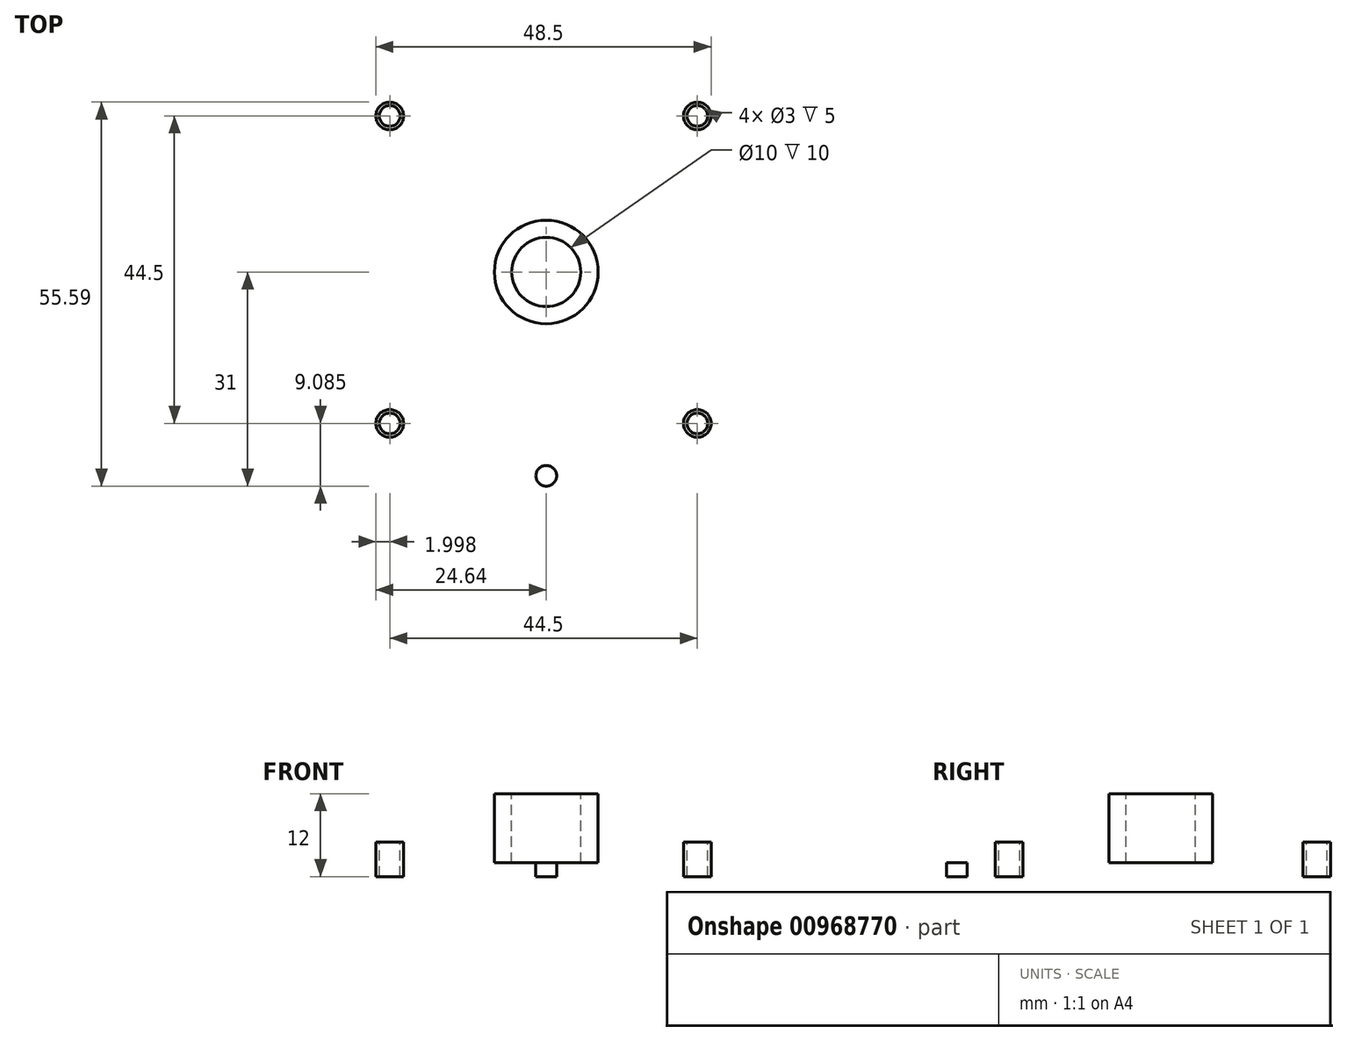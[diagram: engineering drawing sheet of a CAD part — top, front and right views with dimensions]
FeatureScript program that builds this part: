
annotation { "Feature Type Name" : "Feature", "Feature Type Description" : "" }
export const myFeature = defineFeature(function(context is Context, id is Id, definition is map)
    precondition{}
    {
        {
            var Q0;
            Q0=qCreatedBy(makeId("Top.planeOp"),FACE);
            var sketch = newSketch(context, id + "F0", { "sketchPlane" : qUnion([Q0])});
            skLineSegment(sketch, "E0.bottom", {"start": v(25, -25) * mm, "end": v(-25, -25) * mm});
            skLineSegment(sketch, "E0.top", {"start": v(25, 25) * mm, "end": v(-25, 25) * mm});
            skLineSegment(sketch, "E0.left", {"start": v(25, -25) * mm, "end": v(25, 25) * mm});
            skLineSegment(sketch, "E0.right", {"start": v(-25, -25) * mm, "end": v(-25, 25) * mm});
            skPoint(sketch, "E0.middle", {"position": v(0, 0) * mm});
            skSolve(sketch);
        }
        {
            var Q0;
            Q0=makeQuery(id+"F0.imprint","IMPRINT",FACE,{"disambiguationData":[TD([[makeQuery(id+"F0.imprint","IMPRINT",EDGE,{"derivedFrom":sQuery(id+"F0.wireOp",EDGE,"E0.bottom")}),-1.0]])]});
            extrude(context, id + "F1", {"entities" : qUnion([Q0]), "depth" : 2 * mm, "offsetDistance" : 25 * mm});
        }
        {
            var Q0;
            Q0=makeQuery(id+"F1.opExtrude","CAP_FACE",FACE,{"disambiguationData":[OSD([sQuery(id+"F0.wireOp",EDGE,"E0.bottom"),sQuery(id+"F0.wireOp",EDGE,"E0.top"),sQuery(id+"F0.wireOp",EDGE,"E0.left"),sQuery(id+"F0.wireOp",EDGE,"E0.right")])],"isStart":false});
            var sketch = newSketch(context, id + "F2", { "sketchPlane" : qUnion([Q0])});
            skCircle(sketch, "E1", {"center": v(-22.64, 22.59) * mm, "radius": 2 * mm});
            skCircle(sketch, "E2.0.1.0", {"center": v(-22.64, -21.91) * mm, "radius": 2 * mm});
            skCircle(sketch, "E2.1.0.0", {"center": v(21.86, 22.59) * mm, "radius": 2 * mm});
            skCircle(sketch, "E2.1.1.0", {"center": v(21.86, -21.91) * mm, "radius": 2 * mm});
            skLineSegment(sketch, "E2.direction1", {"start": v(-22.64, 22.59) * mm, "end": v(21.86, 22.59) * mm, "construction": true});
            skLineSegment(sketch, "E2.direction2", {"start": v(-22.64, 22.59) * mm, "end": v(-22.64, -21.91) * mm, "construction": true});
            skSolve(sketch);
        }
        {
            var Q0;
            {var subQ0=sQuery(id+"F2.wireOp",EDGE,"E1");var subQ1=makeQuery(id+"F2.imprint","INTERSECT",VERTEX,{"derivedFrom":[makeQuery(id+"F1.opExtrude","CAP_EDGE",EDGE,{"disambiguationData":[OSD([sQuery(id+"F0.wireOp",EDGE,"E0.top")])],"isStart":false}),subQ0]});Q0=makeQuery(id+"F2.imprint","IMPRINT",FACE,{"disambiguationData":[TD([[makeQuery(id+"F2.imprint","IMPRINT",EDGE,{"disambiguationData":[TD([[subQ1,-1.0]])],"derivedFrom":subQ0}),1.0]])]});}
            var Q1;
            Q1=makeQuery(id+"F2.imprint","IMPRINT",FACE,{"disambiguationData":[TD([[makeQuery(id+"F2.imprint","IMPRINT",EDGE,{"derivedFrom":sQuery(id+"F2.wireOp",EDGE,"E2.0.1.0")}),1.0]])]});
            var Q2;
            Q2=makeQuery(id+"F2.imprint","IMPRINT",FACE,{"disambiguationData":[TD([[makeQuery(id+"F2.imprint","IMPRINT",EDGE,{"derivedFrom":sQuery(id+"F2.wireOp",EDGE,"E2.1.1.0")}),1.0]])]});
            var Q3;
            Q3=makeQuery(id+"F2.imprint","IMPRINT",FACE,{"disambiguationData":[TD([[makeQuery(id+"F2.imprint","IMPRINT",EDGE,{"derivedFrom":sQuery(id+"F2.wireOp",EDGE,"E2.1.0.0")}),1.0]])]});
            extrude(context, id + "F3", {"entities" : qUnion([Q0, Q1, Q2, Q3]), "operationType" : NewBodyOperationType.ADD, "depth" : 3 * mm, "offsetDistance" : 25 * mm});
        }
        {
            var Q0;
            Q0=makeQuery(id+"F3.opExtrude","CAP_FACE",FACE,{"disambiguationData":[OSD([sQuery(id+"F2.wireOp",EDGE,"E1")])],"isStart":false});
            var sketch = newSketch(context, id + "F4", { "sketchPlane" : qUnion([Q0])});
            skCircle(sketch, "E3", {"center": v(-22.64, 22.59) * mm, "radius": 1.5 * mm});
            skCircle(sketch, "E4.0.1.0", {"center": v(-22.64, -21.91) * mm, "radius": 1.5 * mm});
            skCircle(sketch, "E4.1.0.0", {"center": v(21.86, 22.59) * mm, "radius": 1.5 * mm});
            skCircle(sketch, "E4.1.1.0", {"center": v(21.86, -21.91) * mm, "radius": 1.5 * mm});
            skLineSegment(sketch, "E4.direction1", {"start": v(-22.64, 22.59) * mm, "end": v(21.86, 22.59) * mm, "construction": true});
            skLineSegment(sketch, "E4.direction2", {"start": v(-22.64, 22.59) * mm, "end": v(-22.64, -21.91) * mm, "construction": true});
            skSolve(sketch);
        }
        {
            var Q0;
            Q0=makeQuery(id+"F4.imprint","IMPRINT",FACE,{"disambiguationData":[TD([[makeQuery(id+"F4.imprint","IMPRINT",EDGE,{"derivedFrom":sQuery(id+"F4.wireOp",EDGE,"E3")}),1.0]])]});
            var Q1;
            Q1=makeQuery(id+"F4.imprint","IMPRINT",FACE,{"disambiguationData":[TD([[makeQuery(id+"F4.imprint","IMPRINT",EDGE,{"derivedFrom":sQuery(id+"F4.wireOp",EDGE,"E4.1.1.0")}),1.0]])]});
            var Q2;
            Q2=makeQuery(id+"F4.imprint","IMPRINT",FACE,{"disambiguationData":[TD([[makeQuery(id+"F4.imprint","IMPRINT",EDGE,{"derivedFrom":sQuery(id+"F4.wireOp",EDGE,"E4.1.0.0")}),1.0]])]});
            var Q3;
            Q3=makeQuery(id+"F4.imprint","IMPRINT",FACE,{"disambiguationData":[TD([[makeQuery(id+"F4.imprint","IMPRINT",EDGE,{"derivedFrom":sQuery(id+"F4.wireOp",EDGE,"E4.0.1.0")}),1.0]])]});
            extrude(context, id + "F5", {"entities" : qUnion([Q0, Q1, Q2, Q3]), "operationType" : NewBodyOperationType.REMOVE, "oppositeDirection" : true, "depth" : 3 * mm, "offsetDistance" : 25 * mm});
        }
        {
            var Q0;
            Q0=qCreatedBy(makeId("Top.planeOp"),FACE);
            var sketch = newSketch(context, id + "F6", { "sketchPlane" : qUnion([Q0])});
            skLineSegment(sketch, "E5.bottom", {"start": v(10.9, 32.5) * mm, "end": v(-10.9, 32.5) * mm});
            skLineSegment(sketch, "E5.left", {"start": v(13.9, 29.5) * mm, "end": v(13.9, 25) * mm});
            skLineSegment(sketch, "E5.right", {"start": v(-13.9, 29.5) * mm, "end": v(-13.9, 25) * mm});
            skPoint(sketch, "E5.middle", {"position": v(0, 25) * mm});
            skLineSegment(sketch, "E6", {"start": v(-13.9, 25) * mm, "end": v(13.9, 25) * mm});
            skPoint(sketch, "E7.visualSharp", {"position": v(-13.9, 32.5) * mm});
            skArc(sketch, "E7.filletArc", {"start": v(-10.9, 32.5) * mm, "mid": v(-13.02, 31.62) * mm, "end": v(-13.9, 29.5) * mm});
            skPoint(sketch, "E8.visualSharp", {"position": v(13.9, 32.5) * mm});
            skArc(sketch, "E8.filletArc", {"start": v(13.9, 29.5) * mm, "mid": v(13.02, 31.62) * mm, "end": v(10.9, 32.5) * mm});
            skLineSegment(sketch, "E9.MirrorCS", {"start": v(-13.9, -25) * mm, "end": v(13.9, -25) * mm});
            skLineSegment(sketch, "E10.MirrorCS", {"start": v(-13.9, -29.5) * mm, "end": v(-13.9, -25) * mm});
            skArc(sketch, "E11.MirrorCS", {"start": v(-10.9, -32.5) * mm, "mid": v(-13.02, -31.62) * mm, "end": v(-13.9, -29.5) * mm});
            skLineSegment(sketch, "E12.MirrorCS", {"start": v(10.9, -32.5) * mm, "end": v(-10.9, -32.5) * mm});
            skArc(sketch, "E13.MirrorCS", {"start": v(13.9, -29.5) * mm, "mid": v(13.02, -31.62) * mm, "end": v(10.9, -32.5) * mm});
            skLineSegment(sketch, "E14.MirrorCS", {"start": v(13.9, -29.5) * mm, "end": v(13.9, -25) * mm});
            skSolve(sketch);
        }
        {
            var Q0;
            Q0=makeQuery(id+"F6.imprint","IMPRINT",FACE,{"disambiguationData":[TD([[makeQuery(id+"F6.imprint","IMPRINT",EDGE,{"derivedFrom":sQuery(id+"F6.wireOp",EDGE,"E5.bottom")}),1.0]])]});
            var Q1;
            Q1=makeQuery(id+"F6.imprint","IMPRINT",FACE,{"disambiguationData":[TD([[makeQuery(id+"F6.imprint","IMPRINT",EDGE,{"derivedFrom":sQuery(id+"F6.wireOp",EDGE,"E9.MirrorCS")}),-1.0]])]});
            extrude(context, id + "F7", {"entities" : qUnion([Q0, Q1]), "operationType" : NewBodyOperationType.ADD, "depth" : 2 * mm, "offsetDistance" : 25 * mm});
        }
        {
            var Q0;
            {var subQ0=sQuery(id+"F0.wireOp",EDGE,"E0.left");var subQ1=sQuery(id+"F0.wireOp",EDGE,"E0.top");var subQ2=sQuery(id+"F0.wireOp",EDGE,"E0.right");var subQ3=sQuery(id+"F0.wireOp",EDGE,"E0.bottom");var subQ4=makeQuery(id+"F1.opExtrude","CAP_FACE",FACE,{"disambiguationData":[OSD([subQ3,subQ1,subQ0,subQ2])],"isStart":false});Q0=makeQuery(id+"F7.boolean.opBoolean","MERGE",FACE,{"derivedFrom":[makeQuery(id+"F3.boolean.opBoolean","SPLIT",FACE,{"disambiguationData":[TD([makeQuery(id+"F1.opExtrude","SWEPT_FACE",FACE,{"disambiguationData":[OSD([subQ3])]}),subQ4,makeQuery(id+"F1.opExtrude","SWEPT_FACE",FACE,{"disambiguationData":[OSD([subQ1])]}),makeQuery(id+"F1.opExtrude","SWEPT_FACE",FACE,{"disambiguationData":[OSD([subQ0])]}),makeQuery(id+"F1.opExtrude","SWEPT_FACE",FACE,{"disambiguationData":[OSD([subQ2])]}),makeQuery(id+"F3.opExtrude","SWEPT_FACE",FACE,{"disambiguationData":[OSD([sQuery(id+"F2.wireOp",EDGE,"E1")])]}),makeQuery(id+"F3.opExtrude","SWEPT_FACE",FACE,{"disambiguationData":[OSD([sQuery(id+"F2.wireOp",EDGE,"E2.0.1.0")])]}),makeQuery(id+"F3.opExtrude","SWEPT_FACE",FACE,{"disambiguationData":[OSD([sQuery(id+"F2.wireOp",EDGE,"E2.1.0.0")])]}),makeQuery(id+"F3.opExtrude","SWEPT_FACE",FACE,{"disambiguationData":[OSD([sQuery(id+"F2.wireOp",EDGE,"E2.1.1.0")])]})])],"derivedFrom":subQ4}),makeQuery(id+"F7.opExtrude","CAP_FACE",FACE,{"disambiguationData":[OSD([sQuery(id+"F6.wireOp",EDGE,"E5.bottom"),sQuery(id+"F6.wireOp",EDGE,"E5.left"),sQuery(id+"F6.wireOp",EDGE,"E5.right"),sQuery(id+"F6.wireOp",EDGE,"E6"),sQuery(id+"F6.wireOp",EDGE,"E7.filletArc"),sQuery(id+"F6.wireOp",EDGE,"E8.filletArc")])],"isStart":false})]});}
            var sketch = newSketch(context, id + "F8", { "sketchPlane" : qUnion([Q0])});
            skCircle(sketch, "E15", {"center": v(0, 29.5) * mm, "radius": 1.5 * mm});
            skCircle(sketch, "E16.MirrorC", {"center": v(0, -29.5) * mm, "radius": 1.5 * mm});
            skSolve(sketch);
        }
        {
            var Q0;
            Q0=makeQuery(id+"F8.imprint","IMPRINT",FACE,{"disambiguationData":[TD([[makeQuery(id+"F8.imprint","IMPRINT",EDGE,{"derivedFrom":sQuery(id+"F8.wireOp",EDGE,"E15")}),1.0]])]});
            var Q1;
            Q1=makeQuery(id+"F8.imprint","IMPRINT",FACE,{"disambiguationData":[TD([[makeQuery(id+"F8.imprint","IMPRINT",EDGE,{"derivedFrom":sQuery(id+"F8.wireOp",EDGE,"E16.MirrorC")}),-1.0]])]});
            extrude(context, id + "F9", {"entities" : qUnion([Q0, Q1]), "operationType" : NewBodyOperationType.REMOVE, "oppositeDirection" : true, "depth" : 25 * mm, "offsetDistance" : 25 * mm});
        }
        {
            var Q0;
            Q0=makeQuery(id+"F7.boolean.opBoolean","MERGE",FACE,{"derivedFrom":[makeQuery(id+"F1.opExtrude","CAP_FACE",FACE,{"disambiguationData":[OSD([sQuery(id+"F0.wireOp",EDGE,"E0.bottom"),sQuery(id+"F0.wireOp",EDGE,"E0.top"),sQuery(id+"F0.wireOp",EDGE,"E0.left"),sQuery(id+"F0.wireOp",EDGE,"E0.right")])],"isStart":false}),makeQuery(id+"F7.opExtrude","CAP_FACE",FACE,{"disambiguationData":[OSD([sQuery(id+"F6.wireOp",EDGE,"E5.bottom"),sQuery(id+"F6.wireOp",EDGE,"E5.left"),sQuery(id+"F6.wireOp",EDGE,"E5.right"),sQuery(id+"F6.wireOp",EDGE,"E6"),sQuery(id+"F6.wireOp",EDGE,"E7.filletArc"),sQuery(id+"F6.wireOp",EDGE,"E8.filletArc")])],"isStart":false}),makeQuery(id+"F7.opExtrude","CAP_FACE",FACE,{"disambiguationData":[OSD([sQuery(id+"F6.wireOp",EDGE,"E9.MirrorCS"),sQuery(id+"F6.wireOp",EDGE,"E10.MirrorCS"),sQuery(id+"F6.wireOp",EDGE,"E11.MirrorCS"),sQuery(id+"F6.wireOp",EDGE,"E12.MirrorCS"),sQuery(id+"F6.wireOp",EDGE,"E13.MirrorCS"),sQuery(id+"F6.wireOp",EDGE,"E14.MirrorCS")])],"isStart":false})]});
            var sketch = newSketch(context, id + "F10", { "sketchPlane" : qUnion([Q0])});
            skCircle(sketch, "E17", {"center": v(0, 0) * mm, "radius": 7.5 * mm});
            skSolve(sketch);
        }
        {
            var Q0;
            Q0=makeQuery(id+"F10.imprint","IMPRINT",FACE,{"disambiguationData":[TD([[makeQuery(id+"F10.imprint","IMPRINT",EDGE,{"derivedFrom":sQuery(id+"F10.wireOp",EDGE,"E17")}),1.0]])]});
            extrude(context, id + "F11", {"entities" : qUnion([Q0]), "operationType" : NewBodyOperationType.ADD, "depth" : 10 * mm, "offsetDistance" : 25 * mm});
        }
        {
            var Q0;
            Q0=makeQuery(id+"F11.opExtrude","CAP_FACE",FACE,{"disambiguationData":[OSD([sQuery(id+"F10.wireOp",EDGE,"E17")])],"isStart":false});
            var sketch = newSketch(context, id + "F12", { "sketchPlane" : qUnion([Q0])});
            skCircle(sketch, "E18", {"center": v(0, 0) * mm, "radius": 5 * mm});
            skSolve(sketch);
        }
        {
            var Q0;
            Q0=makeQuery(id+"F12.imprint","IMPRINT",FACE,{"disambiguationData":[TD([[makeQuery(id+"F12.imprint","IMPRINT",EDGE,{"derivedFrom":sQuery(id+"F12.wireOp",EDGE,"E18")}),1.0]])]});
            extrude(context, id + "F13", {"entities" : qUnion([Q0]), "operationType" : NewBodyOperationType.REMOVE, "oppositeDirection" : true, "depth" : 10 * mm, "offsetDistance" : 25 * mm});
        }
        {
            var Q0;
            Q0=makeQuery(id+"F5.boolean.opBoolean","COPY",FACE,{"derivedFrom":makeQuery(id+"F5.opExtrude","CAP_FACE",FACE,{"disambiguationData":[OSD([sQuery(id+"F4.wireOp",EDGE,"E4.0.1.0")])],"isStart":false})});
            var Q1;
            Q1=makeQuery(id+"F5.boolean.opBoolean","COPY",FACE,{"derivedFrom":makeQuery(id+"F5.opExtrude","CAP_FACE",FACE,{"disambiguationData":[OSD([sQuery(id+"F4.wireOp",EDGE,"E3")])],"isStart":false})});
            var Q2;
            Q2=makeQuery(id+"F5.boolean.opBoolean","COPY",FACE,{"derivedFrom":makeQuery(id+"F5.opExtrude","CAP_FACE",FACE,{"disambiguationData":[OSD([sQuery(id+"F4.wireOp",EDGE,"E4.1.0.0")])],"isStart":false})});
            var Q3;
            Q3=makeQuery(id+"F5.boolean.opBoolean","COPY",FACE,{"derivedFrom":makeQuery(id+"F5.opExtrude","CAP_FACE",FACE,{"disambiguationData":[OSD([sQuery(id+"F4.wireOp",EDGE,"E4.1.1.0")])],"isStart":false})});
            extrude(context, id + "F14", {"entities" : qUnion([Q0, Q1, Q2, Q3]), "operationType" : NewBodyOperationType.REMOVE, "oppositeDirection" : true, "depth" : 7.7 * mm, "offsetDistance" : 25 * mm});
        }
    });
